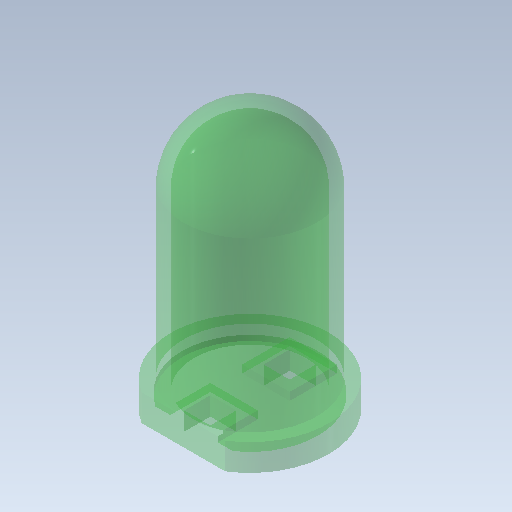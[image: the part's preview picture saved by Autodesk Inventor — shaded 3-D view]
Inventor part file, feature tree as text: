
AUTODESK INVENTOR PART (.ipt)
format: ipt  version: 2020.1 (Build 241239000, 239)  size: 193,024 bytes
history: native  units: mm
features: sketch x2, other x1, revolve x1, plane x1, split x1, extrude x1, shell x1
ambient origin geometry x8: Origin, YZ Plane, XZ Plane, XY Plane, X Axis, Y Axis, Z Axis, Center Point
bodies: Body1 (feature_tree)
feature tree (8):
  other  "Sólido1"
  revolve  "Revolución1"  [1 undecoded]
  plane  "Plano de trabajo1"
  split  "Dividir1"
  extrude  "Extrusión2"  Depth=0.4mm
  shell  "Vaciado1"  Thickness=90.0deg
  sketch  "Boceto1"  dims[d0=2.95mm d1=1.0mm]
  sketch  "Boceto3"  dims[d2=9.7mm d3=5.0mm d5=90.0deg d18=2.5mm d31=1.0mm d32=0.98mm d33=0.98mm d34=1.0mm d35=0.98mm d36=0.0mm d37=0.4mm]
note: 1 required parameter value undecoded (feature->parameter linkage not recoverable at this tier; creation-order binding heuristic only, values carry confidence <= 0.55)
